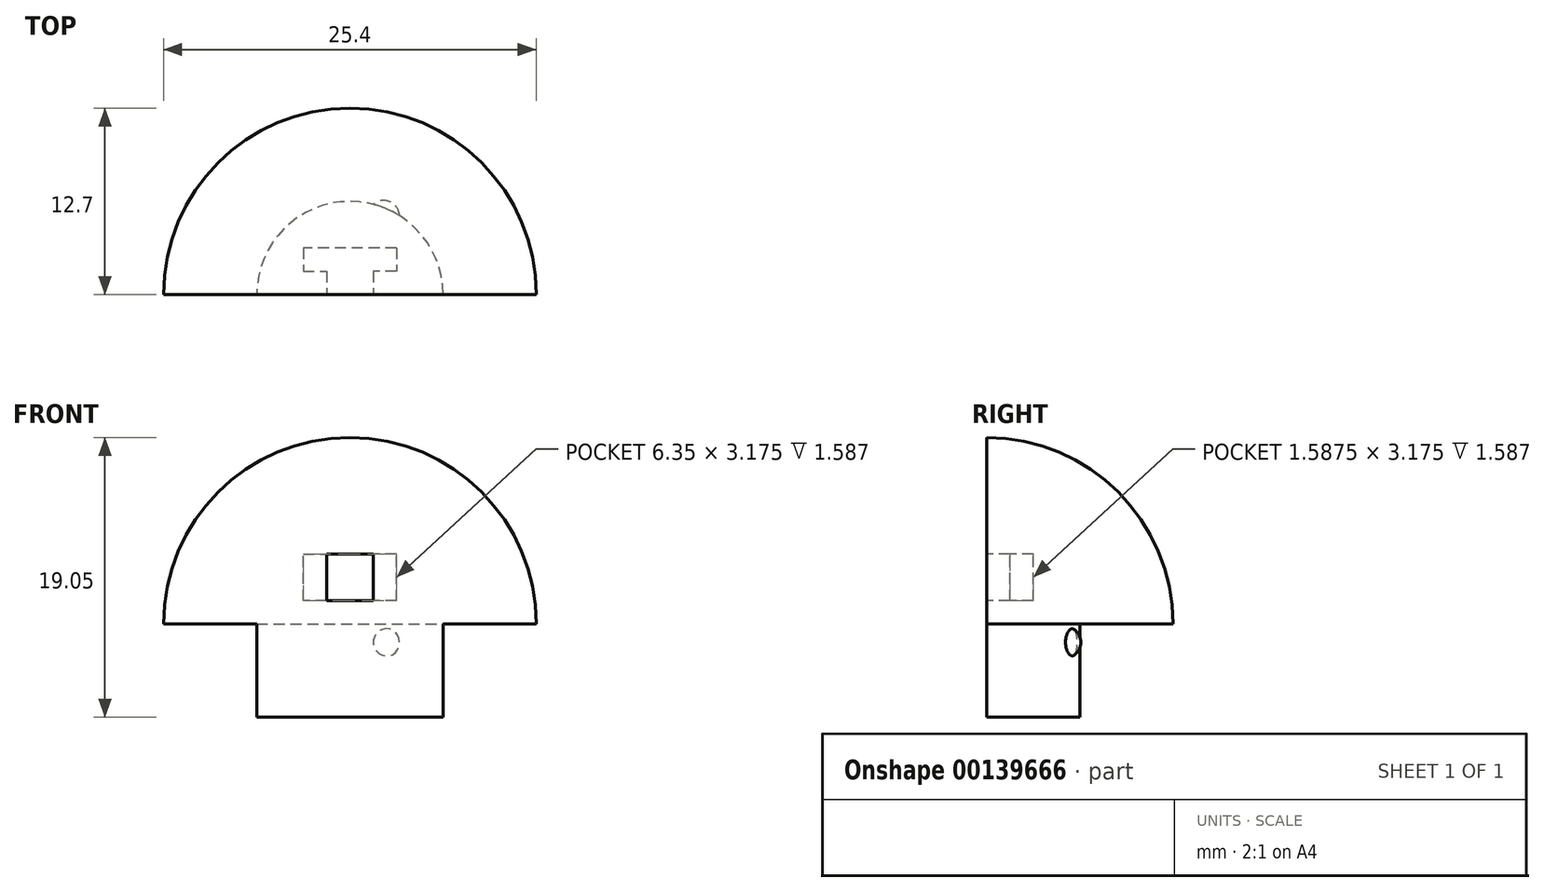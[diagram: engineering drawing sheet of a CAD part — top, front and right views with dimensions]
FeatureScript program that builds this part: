
annotation { "Feature Type Name" : "Feature", "Feature Type Description" : "" }
export const myFeature = defineFeature(function(context is Context, id is Id, definition is map)
    precondition{}
    {
        {
            var Q0;
            Q0=qCreatedBy(makeId("Front.planeOp"),FACE);
            var sketch = newSketch(context, id + "F0", { "sketchPlane" : qUnion([Q0])});
            skArc(sketch, "E0", {"start": v(12.7, 0) * mm, "mid": v(0, 12.7) * mm, "end": v(-12.7, 0) * mm});
            skLineSegment(sketch, "E1", {"start": v(-12.7, 0) * mm, "end": v(-6.35, 0) * mm});
            skLineSegment(sketch, "E2", {"start": v(6.35, 0) * mm, "end": v(12.7, 0) * mm});
            skLineSegment(sketch, "E3.0", {"start": v(-6.35, 0) * mm, "end": v(-6.35, -6.35) * mm});
            skLineSegment(sketch, "E4.0", {"start": v(6.35, 0) * mm, "end": v(6.35, -6.35) * mm});
            skLineSegment(sketch, "E5", {"start": v(6.35, -6.35) * mm, "end": v(-6.35, -6.35) * mm});
            skLineSegment(sketch, "E6", {"start": v(0, 0) * mm, "end": v(0, -6.35) * mm});
            skLineSegment(sketch, "E7", {"start": v(0, -6.35) * mm, "end": v(0, 12.7) * mm});
            skSolve(sketch);
        }
        {
            var Q0;
            {var subQ1=sQuery(id+"F0.wireOp",EDGE,"E4.0");Q0=makeQuery(id+"F0.imprint","IMPRINT",FACE,{"disambiguationData":[TD([[makeQuery(id+"F0.imprint","IMPRINT",EDGE,{"derivedFrom":subQ1}),-1.0]])]});}
            var Q1;
            Q1=sQuery(id+"F0.wireOp",EDGE,"E7");
            revolve(context, id + "F1", {"entities" : qUnion([Q0]), "axis" : qUnion([Q1]), "revolveType" : RevolveType.ONE_DIRECTION, "angle" : 180 * degree});
        }
        {
            var Q0;
            {var subQ1=sQuery(id+"F0.wireOp",EDGE,"E4.0");Q0=makeQuery(id+"F0.imprint","IMPRINT",FACE,{"disambiguationData":[TD([[makeQuery(id+"F0.imprint","IMPRINT",EDGE,{"derivedFrom":subQ1}),-1.0]])]});}
            var sketch = newSketch(context, id + "F2", { "sketchPlane" : qUnion([Q0])});
            skLineSegment(sketch, "E8.bottom", {"start": v(1.59, 1.58) * mm, "end": v(-1.59, 1.58) * mm});
            skLineSegment(sketch, "E8.top", {"start": v(1.59, 4.76) * mm, "end": v(-1.59, 4.76) * mm});
            skLineSegment(sketch, "E8.left", {"start": v(1.59, 1.58) * mm, "end": v(1.59, 4.76) * mm});
            skLineSegment(sketch, "E8.right", {"start": v(-1.59, 1.58) * mm, "end": v(-1.59, 4.76) * mm});
            skPoint(sketch, "E8.middle", {"position": v(0, 3.17) * mm});
            skSolve(sketch);
        }
        {
            var Q0;
            Q0=qSketchRegion(id+"F2",true);
            extrude(context, id + "F3", {"entities" : qUnion([Q0]), "operationType" : NewBodyOperationType.REMOVE, "oppositeDirection" : true, "depth" : 3.17 * mm});
        }
        {
            var Q0;
            Q0=makeQuery(id+"F3.boolean.opBoolean","COPY",FACE,{"derivedFrom":makeQuery(id+"F3.opExtrude","SWEPT_FACE",FACE,{"disambiguationData":[OSD([sQuery(id+"F2.wireOp",EDGE,"E8.left")])]})});
            var sketch = newSketch(context, id + "F4", { "sketchPlane" : qUnion([Q0])});
            skLineSegment(sketch, "E9.bottom", {"start": v(-3.18, 1.58) * mm, "end": v(-1.59, 1.58) * mm});
            skLineSegment(sketch, "E9.top", {"start": v(-3.18, 4.76) * mm, "end": v(-1.59, 4.76) * mm});
            skLineSegment(sketch, "E9.left", {"start": v(-3.18, 1.58) * mm, "end": v(-3.18, 4.76) * mm});
            skLineSegment(sketch, "E9.right", {"start": v(-1.59, 1.58) * mm, "end": v(-1.59, 4.76) * mm});
            skSolve(sketch);
        }
        {
            var Q0;
            Q0=makeQuery(id+"F4.imprint","IMPRINT",FACE,{"disambiguationData":[TD([[makeQuery(id+"F4.imprint","IMPRINT",EDGE,{"derivedFrom":sQuery(id+"F4.wireOp",EDGE,"E9.bottom")}),1.0]])]});
            extrude(context, id + "F5", {"entities" : qUnion([Q0]), "operationType" : NewBodyOperationType.REMOVE, "oppositeDirection" : true, "depth" : 1.59 * mm});
        }
        {
            var Q0;
            Q0=makeQuery(id+"F3.boolean.opBoolean","COPY",FACE,{"derivedFrom":makeQuery(id+"F3.opExtrude","SWEPT_FACE",FACE,{"disambiguationData":[OSD([sQuery(id+"F2.wireOp",EDGE,"E8.right")])]})});
            var sketch = newSketch(context, id + "F6", { "sketchPlane" : qUnion([Q0])});
            skLineSegment(sketch, "E10.bottom", {"start": v(3.18, 1.58) * mm, "end": v(1.59, 1.58) * mm});
            skLineSegment(sketch, "E10.top", {"start": v(3.18, 4.76) * mm, "end": v(1.59, 4.76) * mm});
            skLineSegment(sketch, "E10.left", {"start": v(3.18, 1.58) * mm, "end": v(3.18, 4.76) * mm});
            skLineSegment(sketch, "E10.right", {"start": v(1.59, 1.58) * mm, "end": v(1.59, 4.76) * mm});
            skSolve(sketch);
        }
        {
            var Q0;
            Q0=qSketchRegion(id+"F6",true);
            extrude(context, id + "F7", {"entities" : qUnion([Q0]), "operationType" : NewBodyOperationType.REMOVE, "oppositeDirection" : true, "depth" : 1.59 * mm});
        }
        {
            var Q0;
            Q0=makeQuery(id+"F1.opRevolve","CAP_FACE",FACE,{"disambiguationData":[OSD([sQuery(id+"F0.wireOp",EDGE,"E0"),sQuery(id+"F0.wireOp",EDGE,"E4.0"),sQuery(id+"F0.wireOp",EDGE,"E2"),sQuery(id+"F0.wireOp",EDGE,"E5"),sQuery(id+"F0.wireOp",EDGE,"E7")])],"isStart":false});
            var sketch = newSketch(context, id + "F8", { "sketchPlane" : qUnion([Q0])});
            skCircle(sketch, "E11", {"center": v(2.3, -1.25) * mm, "radius": 1.08 * mm});
            skSolve(sketch);
        }
        {
            var Q0;
            Q0=makeQuery(id+"F8.imprint","IMPRINT",FACE,{"disambiguationData":[TD([[makeQuery(id+"F8.imprint","IMPRINT",EDGE,{"derivedFrom":sQuery(id+"F8.wireOp",EDGE,"E11")}),-1.0]])]});
            cPlane(context, id + "F9", {"entities" : qUnion([Q0]), "cplaneType" : CPlaneType.OFFSET, "offset" : 5.33 * mm, "oppositeDirection" : true, "width" : 152.4 * mm, "height" : 152.4 * mm});
        }
        {
            var Q0;
            Q0=qCreatedBy(id+"F9.planeOp",FACE);
            var sketch = newSketch(context, id + "F10", { "sketchPlane" : qUnion([Q0])});
            skArc(sketch, "E12.0", {"start": v(2.3, -0.17) * mm, "mid": v(1.22, -1.25) * mm, "end": v(2.3, -2.33) * mm});
            skLineSegment(sketch, "E13", {"start": v(2.3, -1.25) * mm, "end": v(2.3, -2.33) * mm});
            skLineSegment(sketch, "E14", {"start": v(2.3, -1.25) * mm, "end": v(2.3, -0.17) * mm});
            skSolve(sketch);
        }
        {
            var Q0;
            Q0 = qSketchRegion(id + "F10", true);
            var Q1;
            Q1=sQuery(id+"F10.wireOp",EDGE,"E13");
            revolve(context, id + "F11", {"operationType" : NewBodyOperationType.ADD, "entities" : qUnion([Q0]), "axis" : qUnion([Q1]), "revolveType" : RevolveType.FULL});
        }
    });
